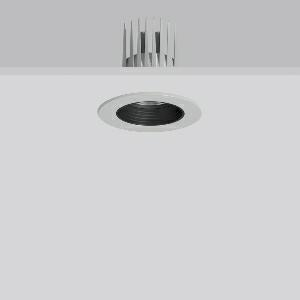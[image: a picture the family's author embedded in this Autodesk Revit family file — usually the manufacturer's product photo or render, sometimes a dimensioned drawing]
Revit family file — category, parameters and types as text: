
# Revit family: heledon_mini_e_901744_004_1_76_fd0a
name_source: partatom
category: Lighting Fixtures
units: mm (PartAtom-declared; Revit-internal decimal feet)

## family parameters
Cut with Voids When Loaded = No
Host = Face
Light Source = No
Part Type = Normal
Room Calculation Point = No
Round Connector Dimension = Use Diameter
Shared = No

## types (1)
- HELEDON mini E (1 x LED Modul 940, 2250 lm, 4000)
    Apparent Load = 20 VA
    Approval mark = CE
    CIE Flux Codes = 96 100 100 100 100
    Color Rendering = 92
    Color Temperature = 4000
    Default Elevation = 1800 mm
    Description = Series: HELEDON mini
Round recessed downlight. Housing: die-cast aluminium, powder-coated. Black plastic ring and recessed LED to prevent glare from the side. Optical assembly with lens made of plastic (polycarbonate) for the best homogeneous light distribution - can be changed without tools. Best colour rendering index Ra>90. Suitable for Recessed ceiling mounting. Installation without tools thanks to spring fastening system. Including separate LED converter with connecting cable 600 mm.High quality converter without flickering and stroboscopic effect. Through-wiring box (5 pole) available as accessory. The following accessories can be mounted without use of tools: interchangeable lenses, decorative glasses, honeycomb louvre, clear and frosted diffusers, white interchangeable plastic ring. 
Colour: silver
Diameter: 124 mm
Height: 3 mm
Cut-out diameter: 114 mm
Recess height: 170 mm
Luminaire: recess height: 120 mm
Lamp: LED
Socket: without socket
Colour temperature: 4000K
Colour rendering index (CRI): 92
System power: 20 W
Rated luminous flux: 2250 lm
Luminous efficiency: 113 lm/W
Control gear: Converter, dimmable, DALI
Protection class: II
Type of protection: IP 20
    Height = 0 mm  [stored 0 ft]
    Lamp = 1 x LED Modul 940
    Lamp Light Flux = 2250 lm
    Lamp count = 1
    Length = 124 mm  [stored 0.406824 ft]
    Lifetime = 50000 h
    Luminous efficacy = 113 lm/W
    Manufacturer = RZB
    ModVariant = No
    Model = 901744.004.1.76
    Mounting Place = Ceiling
    Mounting Type = Recessed
    Number of Poles = 1
    OnlyDefault = Yes
    Power Factor = 1
    Product Name = HELEDON mini E
    Product group = Recessed downlights
    ProductGroupID = 402
    Protection Class = Protection class II
    Protection Degree = IP 20
    RLX_Detail_Level = 1
    RLX_Emergency_Light_Flux = 0 lm
    RLX_Emergency_Type = 0
    RLX_Emergency_Type_DB = No
    RlxData = <blob elided: 129261 chars, md5=397570f5>
    Socket = socket
    Standby Power = 0 W
    System Light Flux = 2250 lm
    System Power = 20 W
    Type Comments = Product without accessories
    Type Image = 901656.004.jpg
    URL = http://relux.com
    VarID = ---
    Voltage = 230 V
    Voltage Range = 220-240 V
    Weight = 0.00 kg
    Width = 0 mm  [stored 0 ft]

note: [stored X ft] marks values corroborated as IEEE doubles in the binary element streams (Revit-internal decimal feet)

## geometry (parser evidence)
native form markers: Blend x4, Sweep x12
no freeform markers — native parametric forms only
